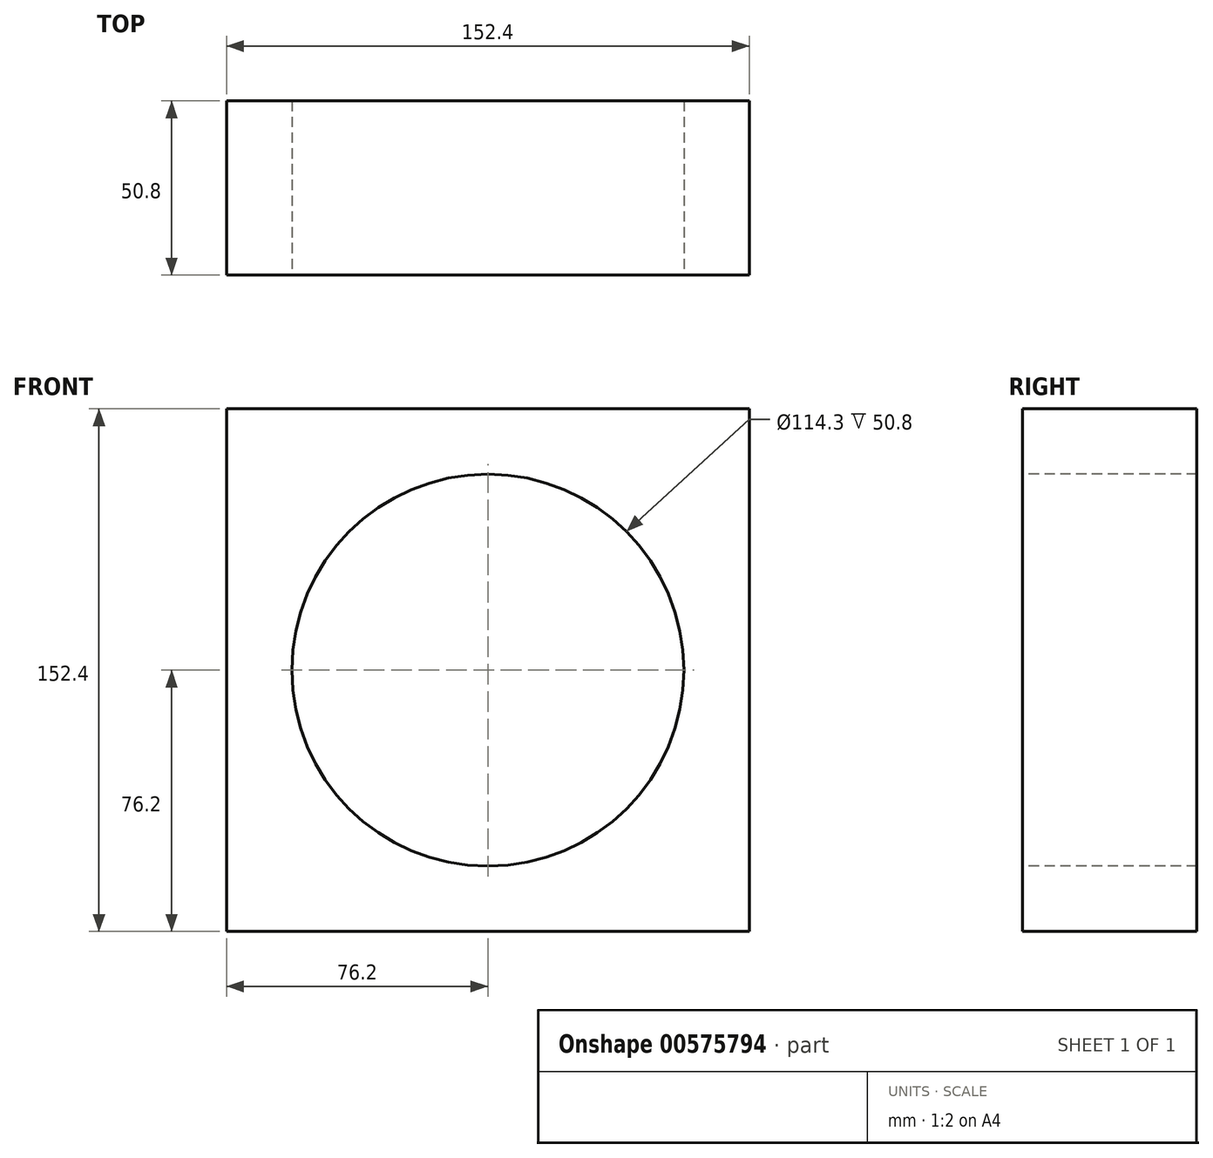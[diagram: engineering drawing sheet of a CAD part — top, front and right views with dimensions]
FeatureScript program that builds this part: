
annotation { "Feature Type Name" : "Feature", "Feature Type Description" : "" }
export const myFeature = defineFeature(function(context is Context, id is Id, definition is map)
    precondition{}
    {
        {
            var Q0;
            Q0=qCreatedBy(makeId("Front.planeOp"),FACE);
            var sketch = newSketch(context, id + "F0", { "sketchPlane" : qUnion([Q0])});
            skLineSegment(sketch, "E0.bottom", {"start": v(0, 0) * mm, "end": v(152.4, 0) * mm});
            skLineSegment(sketch, "E0.top", {"start": v(0, 152.4) * mm, "end": v(152.4, 152.4) * mm});
            skLineSegment(sketch, "E0.left", {"start": v(0, 0) * mm, "end": v(0, 152.4) * mm});
            skLineSegment(sketch, "E0.right", {"start": v(152.4, 0) * mm, "end": v(152.4, 152.4) * mm});
            skSolve(sketch);
        }
        {
            var Q0;
            Q0=makeQuery(id+"F0.imprint","IMPRINT",FACE,{"disambiguationData":[TD([[makeQuery(id+"F0.imprint","IMPRINT",EDGE,{"derivedFrom":sQuery(id+"F0.wireOp",EDGE,"E0.bottom")}),1.0]])]});
            extrude(context, id + "F1", {"entities" : qUnion([Q0]), "depth" : 50.8 * mm, "offsetDistance" : 25.4 * mm});
        }
        {
            var Q0;
            Q0=makeQuery(id+"F1.opExtrude","CAP_FACE",FACE,{"disambiguationData":[OSD([sQuery(id+"F0.wireOp",EDGE,"E0.bottom"),sQuery(id+"F0.wireOp",EDGE,"E0.top"),sQuery(id+"F0.wireOp",EDGE,"E0.left"),sQuery(id+"F0.wireOp",EDGE,"E0.right")])],"isStart":false});
            var sketch = newSketch(context, id + "F2", { "sketchPlane" : qUnion([Q0])});
            skCircle(sketch, "E1", {"center": v(76.2, 76.2) * mm, "radius": 57.15 * mm});
            skPoint(sketch, "E1.centerSnap0", {"position": v(76.2, 0) * mm});
            skPoint(sketch, "E1.centerSnap1", {"position": v(0, 76.2) * mm});
            skSolve(sketch);
        }
        {
            var Q0;
            Q0 = qSketchRegion(id + "F2", true);
            extrude(context, id + "F3", {"entities" : qUnion([Q0]), "operationType" : NewBodyOperationType.REMOVE, "oppositeDirection" : true, "depth" : 50.8 * mm, "offsetDistance" : 25.4 * mm});
        }
    });
